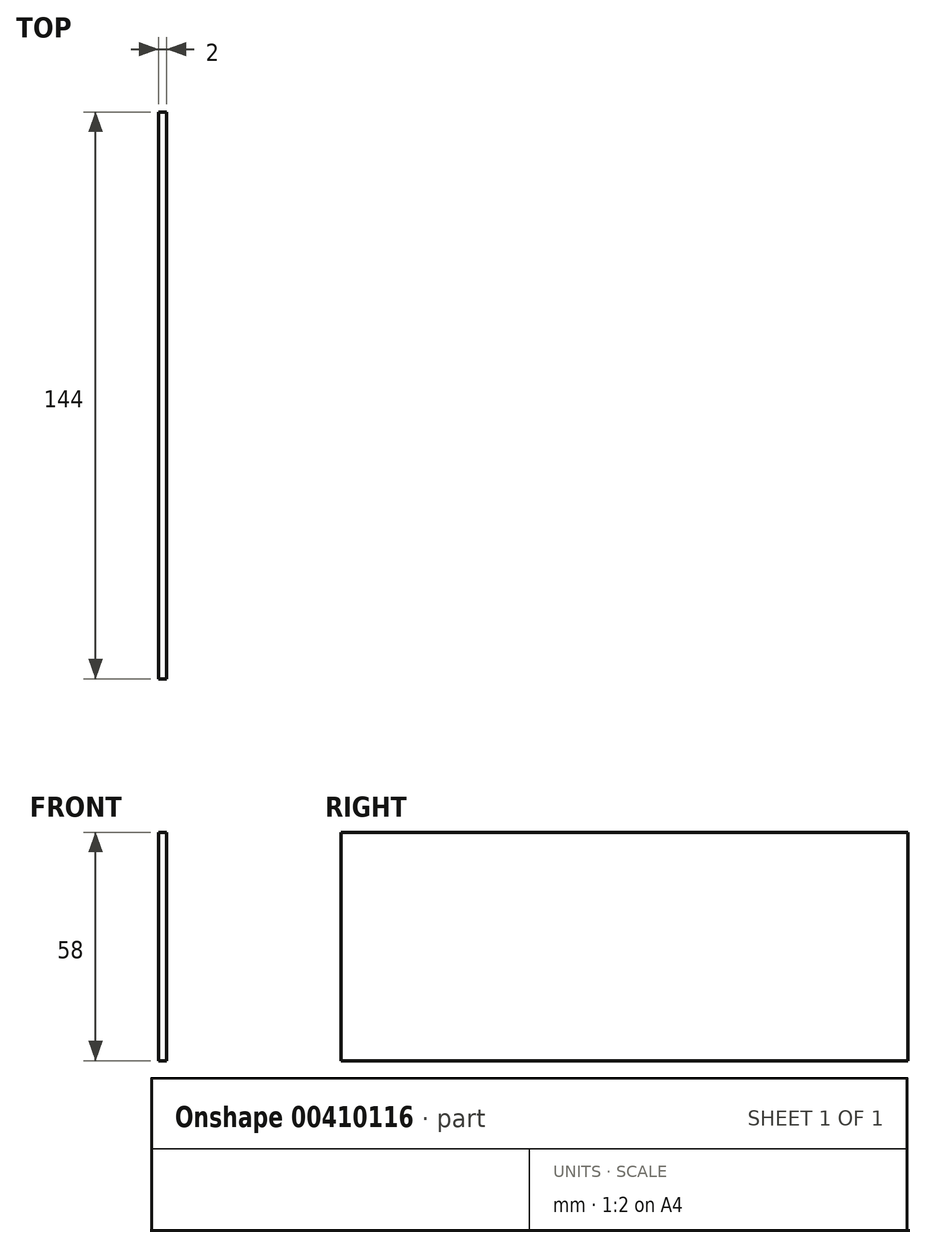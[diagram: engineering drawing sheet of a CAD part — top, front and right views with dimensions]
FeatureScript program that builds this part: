
annotation { "Feature Type Name" : "Feature", "Feature Type Description" : "" }
export const myFeature = defineFeature(function(context is Context, id is Id, definition is map)
    precondition{}
    {
        {
            var Q0;
            Q0=qCreatedBy(makeId("Right.planeOp"),FACE);
            var sketch = newSketch(context, id + "F0", { "sketchPlane" : qUnion([Q0])});
            skLineSegment(sketch, "E0.bottom", {"start": v(0, 0) * mm, "end": v(144, 0) * mm});
            skLineSegment(sketch, "E0.top", {"start": v(0, 58) * mm, "end": v(144, 58) * mm});
            skLineSegment(sketch, "E0.left", {"start": v(0, 0) * mm, "end": v(0, 58) * mm});
            skLineSegment(sketch, "E0.right", {"start": v(144, 0) * mm, "end": v(144, 58) * mm});
            skSolve(sketch);
        }
        {
            var Q0;
            Q0=makeQuery(id+"F0.imprint","IMPRINT",FACE,{"disambiguationData":[TD([[makeQuery(id+"F0.imprint","IMPRINT",EDGE,{"derivedFrom":sQuery(id+"F0.wireOp",EDGE,"E0.bottom")}),1.0]])]});
            extrude(context, id + "F1", {"entities" : qUnion([Q0]), "depth" : 2 * mm});
        }
    });
